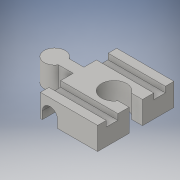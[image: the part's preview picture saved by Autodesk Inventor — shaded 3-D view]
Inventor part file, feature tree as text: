
AUTODESK INVENTOR PART (.ipt)
format: ipt  version: 2016 (Build 200138000, 138)  size: 148,480 bytes
history: native  units: in
note: dims shown in document units (in); Inventor stores cm internally (conversion verified against a paired STEP export)
features: extrude x3, sketch x3
ambient origin geometry x8: Origin, YZ Plane, XZ Plane, XY Plane, X Axis, Y Axis, Z Axis, Center Point
bodies: Solid1 (feature_tree)
feature tree (6):
  extrude  "Extrusion1"  Depth=1.5748in
  extrude  "Extrusion2"  Depth=0.6772in
  extrude  "Extrusion3"  Depth=0.3543in
  sketch  "Sketch1"  dims[d0=1.1811in d1=1.5748in]
  sketch  "Sketch2"  dims[d2=0.6772in d5=0.6772in]
  sketch  "Sketch3"  dims[d6=0.315in d8=0.5118in d10=0.4921in d12=0.3058in d17=0.5217in d18=0.7874in d19=0.6496in d20=0.6496in d21=0.4478in d22=0.4685in d23=0.0in d24=0.2402in d25=0.1772in d26=0.2402in d27=0.1772in d28=0.1181in d29=0.0in d31=0.1181in d32=0.0in d34=0.3543in d35=0.0in]
